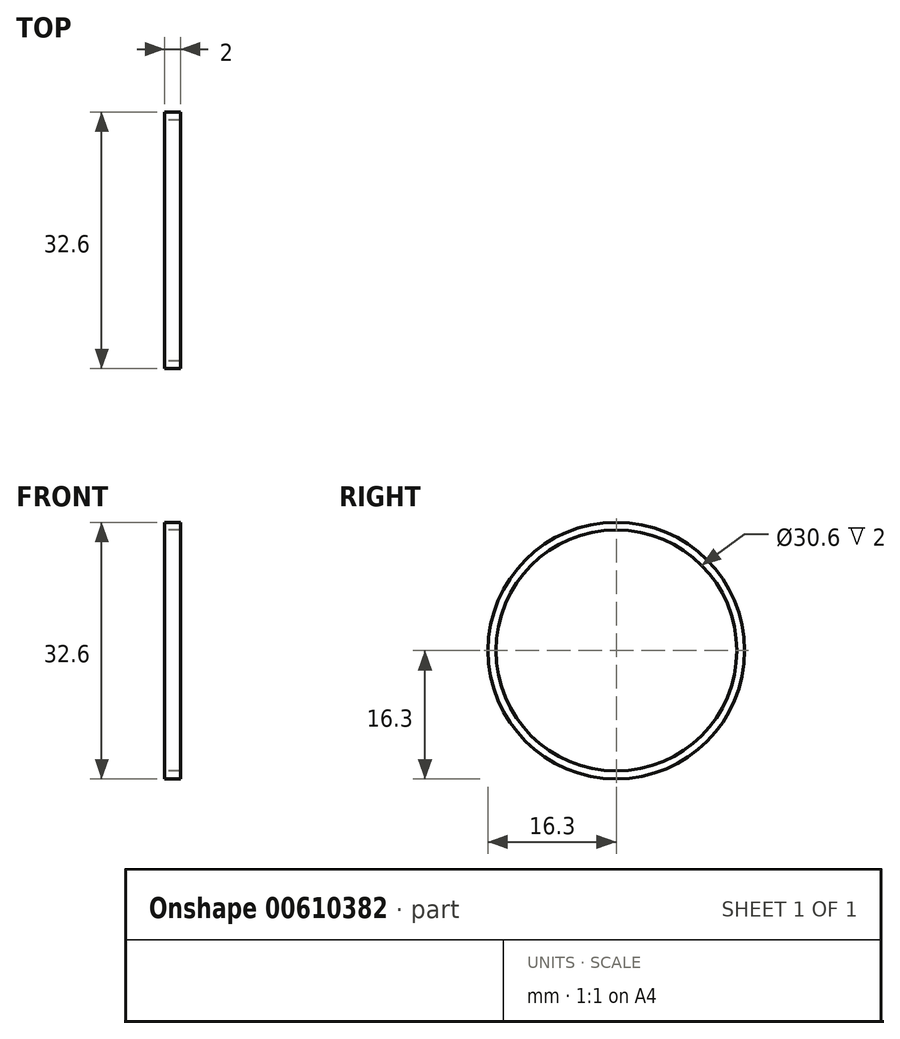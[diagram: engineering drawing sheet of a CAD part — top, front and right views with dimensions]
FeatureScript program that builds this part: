
annotation { "Feature Type Name" : "Feature", "Feature Type Description" : "" }
export const myFeature = defineFeature(function(context is Context, id is Id, definition is map)
    precondition{}
    {
        {
            var Q0;
            Q0=qCreatedBy(makeId("Front.planeOp"),FACE);
            var sketch = newSketch(context, id + "F0", { "sketchPlane" : qUnion([Q0])});
            skLineSegment(sketch, "E0.bottom", {"start": v(-1, 16.3) * mm, "end": v(1, 16.3) * mm});
            skLineSegment(sketch, "E0.top", {"start": v(-1, 15.3) * mm, "end": v(1, 15.3) * mm});
            skLineSegment(sketch, "E0.left", {"start": v(-1, 16.3) * mm, "end": v(-1, 15.3) * mm});
            skLineSegment(sketch, "E0.right", {"start": v(1, 16.3) * mm, "end": v(1, 15.3) * mm});
            skLineSegment(sketch, "E1", {"start": v(-9.6, 0) * mm, "end": v(11.39, 0) * mm});
            skSolve(sketch);
        }
        {
            var Q0;
            Q0=makeQuery(id+"F0.imprint","IMPRINT",FACE,{"disambiguationData":[TD([[makeQuery(id+"F0.imprint","IMPRINT",EDGE,{"derivedFrom":sQuery(id+"F0.wireOp",EDGE,"E0.bottom")}),-1.0]])]});
            var Q1;
            Q1=sQuery(id+"F0.wireOp",EDGE,"E1");
            revolve(context, id + "F1", {"entities" : qUnion([Q0]), "axis" : qUnion([Q1]), "revolveType" : RevolveType.FULL});
        }
    });
